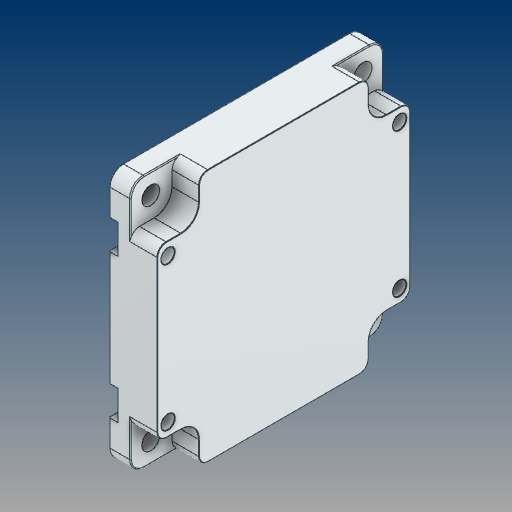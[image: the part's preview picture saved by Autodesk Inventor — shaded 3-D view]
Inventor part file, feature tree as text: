
AUTODESK INVENTOR PART (.ipt)
format: ipt  version: 2021 (Build 250183000, 183)  size: 243,712 bytes
history: native  units: mm
features: chamfer x1
ambient origin geometry x8: Origin, YZ Plane, XZ Plane, XY Plane, X Axis, Y Axis, Z Axis, Center Point
bodies: Solid1 (feature_tree)
feature tree (1):
  chamfer  "Chamfer3"  [1 undecoded]
note: 1 required parameter value undecoded (feature->parameter linkage not recoverable at this tier; creation-order binding heuristic only, values carry confidence <= 0.55)
